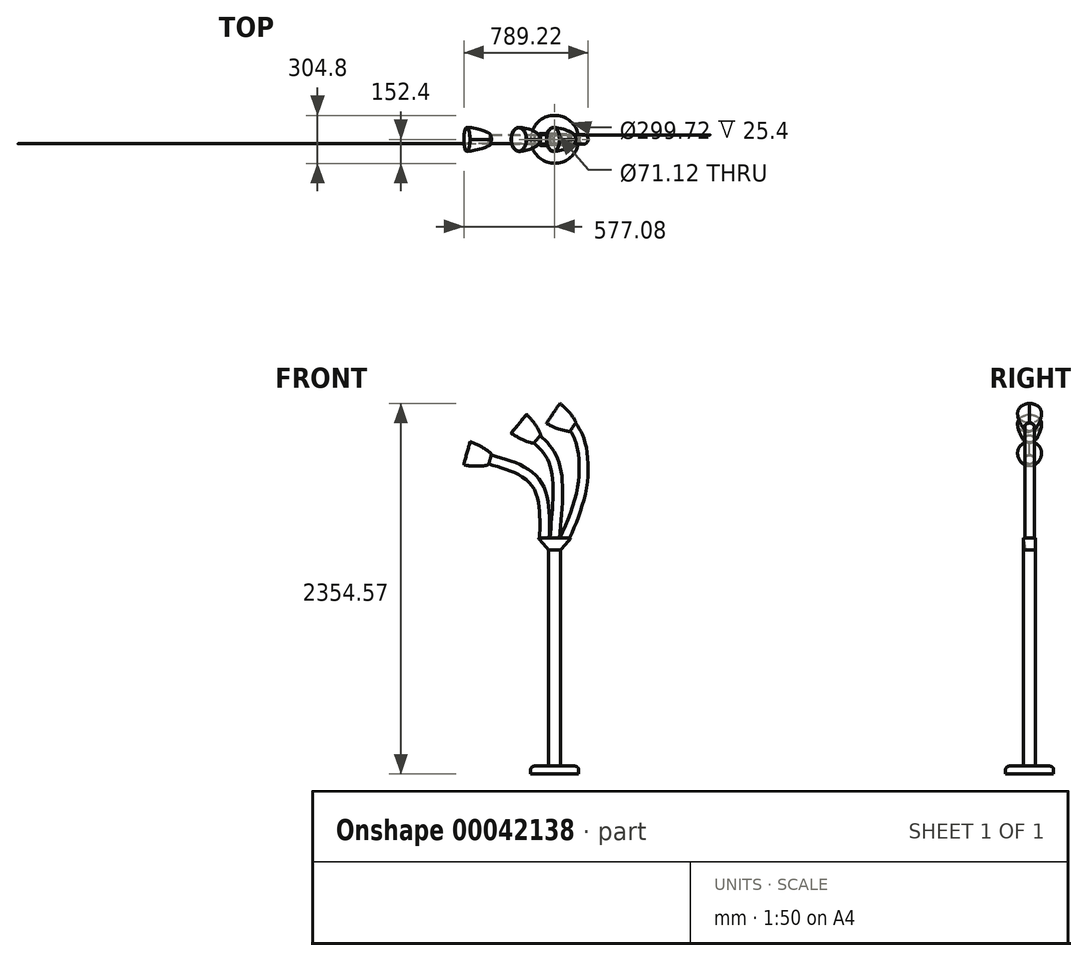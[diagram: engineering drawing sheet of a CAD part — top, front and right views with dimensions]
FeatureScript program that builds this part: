
annotation { "Feature Type Name" : "Feature", "Feature Type Description" : "" }
export const myFeature = defineFeature(function(context is Context, id is Id, definition is map)
    precondition{}
    {
        {
            var Q0;
            Q0=qCreatedBy(makeId("Top.planeOp"),FACE);
            var sketch = newSketch(context, id + "F0", { "sketchPlane" : qUnion([Q0])});
            skCircle(sketch, "E0", {"center": v(0, 0) * mm, "radius": 152.4 * mm});
            skSolve(sketch);
        }
        {
            var Q0;
            Q0=makeQuery(id+"F0.imprint","IMPRINT",FACE,{"disambiguationData":[TD([[makeQuery(id+"F0.imprint","IMPRINT",EDGE,{"derivedFrom":sQuery(id+"F0.wireOp",EDGE,"E0")}),1.0]])]});
            extrude(context, id + "F1", {"entities" : qUnion([Q0]), "depth" : 50.8 * mm});
        }
        {
            var Q0;
            Q0=makeQuery(id+"F1.opExtrude","CAP_EDGE",EDGE,{"disambiguationData":[OSD([sQuery(id+"F0.wireOp",EDGE,"E0")])],"isStart":false});
            fillet(context, id + "F2", {"entities" : qUnion([Q0]), "radius" : 22.86 * mm, "tangentPropagation" : true, "allowEdgeOverflow" : false});
        }
        {
            var Q0;
            Q0=makeQuery(id+"F1.opExtrude","CAP_FACE",FACE,{"disambiguationData":[OSD([sQuery(id+"F0.wireOp",EDGE,"E0")])],"isStart":false});
            var sketch = newSketch(context, id + "F3", { "sketchPlane" : qUnion([Q0])});
            skCircle(sketch, "E1", {"center": v(0, 0) * mm, "radius": 38.1 * mm});
            skSolve(sketch);
        }
        {
            var Q0;
            Q0=makeQuery(id+"F3.imprint","IMPRINT",FACE,{"disambiguationData":[TD([[makeQuery(id+"F3.imprint","IMPRINT",EDGE,{"derivedFrom":sQuery(id+"F3.wireOp",EDGE,"E1")}),1.0]])]});
            extrude(context, id + "F4", {"entities" : qUnion([Q0]), "operationType" : NewBodyOperationType.ADD, "depth" : 1371.6 * mm});
        }
        {
            var Q0;
            Q0=makeQuery(id+"F4.opExtrude","CAP_FACE",FACE,{"disambiguationData":[OSD([sQuery(id+"F3.wireOp",EDGE,"E1")])],"isStart":false});
            cPlane(context, id + "F5", {"entities" : qUnion([Q0]), "cplaneType" : CPlaneType.OFFSET, "offset" : 76.2 * mm, "width" : 152.4 * mm, "height" : 152.4 * mm});
        }
        {
            var Q0;
            Q0=qCreatedBy(id+"F5.planeOp",FACE);
            var sketch = newSketch(context, id + "F6", { "sketchPlane" : qUnion([Q0])});
            skLineSegment(sketch, "E2.bottom", {"start": v(0, 38.1) * mm, "end": v(0, 38.1) * mm});
            skLineSegment(sketch, "E2.top", {"start": v(0, -38.1) * mm, "end": v(0, -38.1) * mm});
            skLineSegment(sketch, "E2.left", {"start": v(0, 38.1) * mm, "end": v(0, -38.1) * mm, "construction": true});
            skLineSegment(sketch, "E2.right", {"start": v(0, 38.1) * mm, "end": v(0, -38.1) * mm, "construction": true});
            skLineSegment(sketch, "E3", {"start": v(0, 38.1) * mm, "end": v(88.9, 38.1) * mm});
            skLineSegment(sketch, "E4", {"start": v(101.6, 25.4) * mm, "end": v(101.6, -25.4) * mm});
            skLineSegment(sketch, "E5", {"start": v(88.9, -38.1) * mm, "end": v(0, -38.1) * mm});
            skLineSegment(sketch, "E6", {"start": v(0, -38.1) * mm, "end": v(-88.9, -38.1) * mm});
            skLineSegment(sketch, "E7", {"start": v(-101.6, -25.4) * mm, "end": v(-101.6, 25.4) * mm});
            skLineSegment(sketch, "E8", {"start": v(-88.9, 38.1) * mm, "end": v(0, 38.1) * mm});
            skPoint(sketch, "E9.visualSharp", {"position": v(101.6, 38.1) * mm});
            skArc(sketch, "E9.filletArc", {"start": v(101.6, 25.4) * mm, "mid": v(97.88, 34.38) * mm, "end": v(88.9, 38.1) * mm});
            skPoint(sketch, "E10.visualSharp", {"position": v(101.6, -38.1) * mm});
            skArc(sketch, "E10.filletArc", {"start": v(88.9, -38.1) * mm, "mid": v(97.88, -34.38) * mm, "end": v(101.6, -25.4) * mm});
            skPoint(sketch, "E11.visualSharp", {"position": v(-101.6, -38.1) * mm});
            skArc(sketch, "E11.filletArc", {"start": v(-101.6, -25.4) * mm, "mid": v(-97.88, -34.38) * mm, "end": v(-88.9, -38.1) * mm});
            skPoint(sketch, "E12.visualSharp", {"position": v(-101.6, 38.1) * mm});
            skArc(sketch, "E12.filletArc", {"start": v(-88.9, 38.1) * mm, "mid": v(-97.88, 34.38) * mm, "end": v(-101.6, 25.4) * mm});
            skSolve(sketch);
        }
        {
            var Q0;
            Q0=makeQuery(id+"F4.opExtrude","CAP_FACE",FACE,{"disambiguationData":[OSD([sQuery(id+"F3.wireOp",EDGE,"E1")])],"isStart":false});
            var sketch = newSketch(context, id + "F7", { "sketchPlane" : qUnion([Q0])});
            skArc(sketch, "E13", {"start": v(-27.2, 26.68) * mm, "mid": v(-38.1, 0.43) * mm, "end": v(-27.8, -26.06) * mm});
            skArc(sketch, "E14", {"start": v(-27.8, -26.06) * mm, "mid": v(1, -38.09) * mm, "end": v(29.12, -24.57) * mm});
            skArc(sketch, "E15", {"start": v(29.12, -24.57) * mm, "mid": v(38.04, 2.06) * mm, "end": v(26.3, 27.57) * mm});
            skArc(sketch, "E16", {"start": v(26.3, 27.57) * mm, "mid": v(-0.64, 38.1) * mm, "end": v(-27.2, 26.68) * mm});
            skSolve(sketch);
        }
        {
            var Q1;
            Q1=makeQuery(id+"F7.imprint","IMPRINT",FACE,{"disambiguationData":[TD([[makeQuery(id+"F7.imprint","IMPRINT",EDGE,{"derivedFrom":sQuery(id+"F7.wireOp",EDGE,"E13")}),1.0]])]});
            var Q2;
            Q2=makeQuery(id+"F6.imprint","IMPRINT",FACE,{"disambiguationData":[TD([[makeQuery(id+"F6.imprint","IMPRINT",EDGE,{"derivedFrom":sQuery(id+"F6.wireOp",EDGE,"E3")}),-1.0]])]});
            var Q3;
            Q3=sQuery(id+"F7.wireOp",VERTEX,"E15.start");
            var Q4;
            Q4=sQuery(id+"F6.wireOp",VERTEX,"E5.start");
            loft(context, id + "F8", {"operationType" : NewBodyOperationType.ADD, "sheetProfilesArray" : [{ "sheetProfileEntities" : qUnion([Q1]) }, { "sheetProfileEntities" : qUnion([Q2]) }], "matchConnections" : true, "connections" : [{ "connectionEntities" : qUnion([Q3, Q4]), "connectionEdgeQueries" : qUnion([]), "connectionEdgeParameters" : [] }]});
        }
        {
            var Q0;
            Q0=makeQuery(id+"F8.opLoft","CAP_FACE",FACE,{"disambiguationData":[OSD([makeQuery(id+"F6.imprint","IMPRINT",FACE,{"disambiguationData":[TD([[makeQuery(id+"F6.imprint","IMPRINT",EDGE,{"derivedFrom":sQuery(id+"F6.wireOp",EDGE,"E3")}),-1.0]])]})])],"isStart":true});
            var sketch = newSketch(context, id + "F9", { "sketchPlane" : qUnion([Q0])});
            skCircle(sketch, "E17", {"center": v(64.74, 0) * mm, "radius": 30.45 * mm});
            skCircle(sketch, "E18", {"center": v(0, 0) * mm, "radius": 30.45 * mm});
            skCircle(sketch, "E19", {"center": v(-64.74, 0) * mm, "radius": 30.45 * mm});
            skLineSegment(sketch, "E20", {"start": v(64.74, 0) * mm, "end": v(0, 0) * mm});
            skLineSegment(sketch, "E21", {"start": v(0, 0) * mm, "end": v(-64.74, 0) * mm});
            skSolve(sketch);
        }
        {
            var Q0;
            Q0=qCreatedBy(makeId("Front.planeOp"),FACE);
            var sketch = newSketch(context, id + "F10", { "sketchPlane" : qUnion([Q0])});
            skCircle(sketch, "E22", {"center": v(0, 0) * mm, "radius": 24.83 * mm});
            skCircle(sketch, "E23", {"center": v(-62.86, 0) * mm, "radius": 24.83 * mm});
            skCircle(sketch, "E24", {"center": v(62.86, 0) * mm, "radius": 24.83 * mm});
            skLineSegment(sketch, "E25", {"start": v(62.86, 0) * mm, "end": v(0, 0) * mm, "construction": true});
            skLineSegment(sketch, "E26", {"start": v(0, 0) * mm, "end": v(-62.86, 0) * mm, "construction": true});
            skFitSpline(sketch, "E27", {"points": [v(0, 1498.72) * mm, v(0, 1966.96) * mm, v(-110.42, 2128.4) * mm], "startDerivative": vector(85.42, 880.08) * mm, "endDerivative": vector(-336.47, 340.63) * mm});
            skFitSpline(sketch, "E28", {"points": [v(-64.74, 1498.6) * mm, v(-119.82, 1851.4) * mm, v(-410.2, 1998.5) * mm], "startDerivative": vector(15.1, 783.93) * mm, "endDerivative": vector(-712.02, 206.42) * mm});
            skFitSpline(sketch, "E29", {"points": [v(64.74, 1498.6) * mm, v(173.73, 1819.38) * mm, v(164.83, 2105.76) * mm, v(116.29, 2205.3) * mm], "startDerivative": vector(322.12, 770.87) * mm, "endDerivative": vector(-235.51, 362.9) * mm});
            skSolve(sketch);
        }
        {
            var Q0;
            Q0=makeQuery(id+"F9.imprint","IMPRINT",FACE,{"disambiguationData":[TD([[makeQuery(id+"F9.imprint","IMPRINT",EDGE,{"derivedFrom":sQuery(id+"F9.wireOp",EDGE,"E17")}),1.0]])]});
            var Q1;
            Q1=sQuery(id+"F10.wireOp",EDGE,"E29");
            sweep(context, id + "F11", {"operationType" : NewBodyOperationType.ADD, "profiles" : qUnion([Q0]), "path" : qUnion([Q1])});
        }
        {
            var Q0;
            {var subQ1=sQuery(id+"F9.wireOp",EDGE,"E18");var subQ3=sQuery(id+"F9.wireOp",EDGE,"E20");var subQ5=makeQuery(id+"F9.imprint","INTERSECT",VERTEX,{"derivedFrom":[subQ1,subQ3]});Q0=makeQuery(id+"F9.imprint","IMPRINT",FACE,{"disambiguationData":[TD([[makeQuery(id+"F9.imprint","IMPRINT",EDGE,{"disambiguationData":[TD([[subQ5,1.0]])],"derivedFrom":subQ1}),1.0]])]});}
            var Q1;
            {var subQ1=sQuery(id+"F9.wireOp",EDGE,"E18");var subQ3=sQuery(id+"F9.wireOp",EDGE,"E20");var subQ5=makeQuery(id+"F9.imprint","INTERSECT",VERTEX,{"derivedFrom":[subQ1,subQ3]});Q1=makeQuery(id+"F9.imprint","IMPRINT",FACE,{"disambiguationData":[TD([[makeQuery(id+"F9.imprint","IMPRINT",EDGE,{"disambiguationData":[TD([[subQ5,-1.0]])],"derivedFrom":subQ1}),1.0]])]});}
            var Q2;
            Q2=sQuery(id+"F10.wireOp",EDGE,"E27");
            sweep(context, id + "F12", {"operationType" : NewBodyOperationType.ADD, "profiles" : qUnion([Q0, Q1]), "path" : qUnion([Q2])});
        }
        {
            var Q0;
            Q0=makeQuery(id+"F9.imprint","IMPRINT",FACE,{"disambiguationData":[TD([[makeQuery(id+"F9.imprint","IMPRINT",EDGE,{"derivedFrom":sQuery(id+"F9.wireOp",EDGE,"E19")}),1.0]])]});
            var Q1;
            Q1=sQuery(id+"F10.wireOp",EDGE,"E28");
            sweep(context, id + "F13", {"operationType" : NewBodyOperationType.ADD, "profiles" : qUnion([Q0]), "path" : qUnion([Q1])});
        }
        {
            var Q0;
            Q0=makeQuery(id+"F11.opSweep","CAP_FACE",FACE,{"disambiguationData":[OSD([sQuery(id+"F9.wireOp",EDGE,"E17"),sQuery(id+"F10.wireOp",VERTEX,"E29.end")])],"isStart":false});
            cPlane(context, id + "F14", {"entities" : qUnion([Q0]), "cplaneType" : CPlaneType.OFFSET, "offset" : 152.4 * mm, "width" : 152.4 * mm, "height" : 152.4 * mm});
        }
        {
            var Q0;
            Q0=qCreatedBy(id+"F14.planeOp",FACE);
            var sketch = newSketch(context, id + "F15", { "sketchPlane" : qUnion([Q0])});
            skCircle(sketch, "E30", {"center": v(-0.19, 1887) * mm, "radius": 76.2 * mm});
            skSolve(sketch);
        }
        {
            var Q1;
            Q1=makeQuery(id+"F11.opSweep","CAP_FACE",FACE,{"disambiguationData":[OSD([sQuery(id+"F9.wireOp",EDGE,"E17"),sQuery(id+"F10.wireOp",VERTEX,"E29.end")])],"isStart":false});
            var Q2;
            Q2=makeQuery(id+"F15.imprint","IMPRINT",FACE,{"disambiguationData":[TD([[makeQuery(id+"F15.imprint","IMPRINT",EDGE,{"derivedFrom":sQuery(id+"F15.wireOp",EDGE,"E30")}),1.0]])]});
            loft(context, id + "F16", {"startCondition" : LoftEndDerivativeType.TANGENT_TO_PROFILE, "startMagnitude" : 1, "endCondition" : LoftEndDerivativeType.NORMAL_TO_PROFILE, "endMagnitude" : 1, "sheetProfilesArray" : [{ "sheetProfileEntities" : qUnion([Q1]) }, { "sheetProfileEntities" : qUnion([Q2]) }]});
        }
        {
            var Q0;
            Q0=makeQuery(id+"F12.opSweep","CAP_FACE",FACE,{"disambiguationData":[OSD([sQuery(id+"F9.wireOp",EDGE,"E18"),sQuery(id+"F10.wireOp",VERTEX,"E27.end")])],"isStart":false});
            cPlane(context, id + "F17", {"entities" : qUnion([Q0]), "cplaneType" : CPlaneType.OFFSET, "offset" : 152.4 * mm, "width" : 152.4 * mm, "height" : 152.4 * mm});
        }
        {
            var Q0;
            Q0=qCreatedBy(id+"F17.planeOp",FACE);
            var sketch = newSketch(context, id + "F18", { "sketchPlane" : qUnion([Q0])});
            skCircle(sketch, "E31", {"center": v(0.03, 1564.34) * mm, "radius": 76.2 * mm});
            skSolve(sketch);
        }
        {
            var Q0;
            Q0=makeQuery(id+"F13.opSweep","CAP_FACE",FACE,{"disambiguationData":[OSD([sQuery(id+"F9.wireOp",EDGE,"E19"),sQuery(id+"F10.wireOp",VERTEX,"E28.end")])],"isStart":false});
            cPlane(context, id + "F19", {"entities" : qUnion([Q0]), "cplaneType" : CPlaneType.OFFSET, "offset" : 152.4 * mm, "width" : 152.4 * mm, "height" : 152.4 * mm});
        }
        {
            var Q0;
            Q0=qCreatedBy(id+"F19.planeOp",FACE);
            var sketch = newSketch(context, id + "F20", { "sketchPlane" : qUnion([Q0])});
            skCircle(sketch, "E32", {"center": v(-0.07, 1823.6) * mm, "radius": 76.2 * mm});
            skSolve(sketch);
        }
        {
            var Q1;
            Q1=makeQuery(id+"F12.opSweep","CAP_FACE",FACE,{"disambiguationData":[OSD([sQuery(id+"F9.wireOp",EDGE,"E18"),sQuery(id+"F10.wireOp",VERTEX,"E27.end")])],"isStart":false});
            var Q2;
            Q2=makeQuery(id+"F18.imprint","IMPRINT",FACE,{"disambiguationData":[TD([[makeQuery(id+"F18.imprint","IMPRINT",EDGE,{"derivedFrom":sQuery(id+"F18.wireOp",EDGE,"E31")}),1.0]])]});
            loft(context, id + "F21", {"operationType" : NewBodyOperationType.ADD, "startCondition" : LoftEndDerivativeType.TANGENT_TO_PROFILE, "startMagnitude" : 1, "endCondition" : LoftEndDerivativeType.NORMAL_TO_PROFILE, "endMagnitude" : 1, "sheetProfilesArray" : [{ "sheetProfileEntities" : qUnion([Q1]) }, { "sheetProfileEntities" : qUnion([Q2]) }]});
        }
        {
            var Q1;
            Q1=makeQuery(id+"F13.opSweep","CAP_FACE",FACE,{"disambiguationData":[OSD([sQuery(id+"F9.wireOp",EDGE,"E19"),sQuery(id+"F10.wireOp",VERTEX,"E28.end")])],"isStart":false});
            var Q2;
            Q2=makeQuery(id+"F20.imprint","IMPRINT",FACE,{"disambiguationData":[TD([[makeQuery(id+"F20.imprint","IMPRINT",EDGE,{"derivedFrom":sQuery(id+"F20.wireOp",EDGE,"E32")}),1.0]])]});
            loft(context, id + "F22", {"startCondition" : LoftEndDerivativeType.TANGENT_TO_PROFILE, "startMagnitude" : 1, "endCondition" : LoftEndDerivativeType.NORMAL_TO_PROFILE, "endMagnitude" : 1, "sheetProfilesArray" : [{ "sheetProfileEntities" : qUnion([Q1]) }, { "sheetProfileEntities" : qUnion([Q2]) }]});
        }
        {
            var Q0;
            Q0=makeQuery(id+"F22.opLoft","CAP_FACE",FACE,{"disambiguationData":[OSD([makeQuery(id+"F20.imprint","IMPRINT",FACE,{"disambiguationData":[TD([[makeQuery(id+"F20.imprint","IMPRINT",EDGE,{"derivedFrom":sQuery(id+"F20.wireOp",EDGE,"E32")}),1.0]])]})])],"isStart":true});
            var Q1;
            Q1=makeQuery(id+"F21.opLoft","CAP_FACE",FACE,{"disambiguationData":[OSD([makeQuery(id+"F18.imprint","IMPRINT",FACE,{"disambiguationData":[TD([[makeQuery(id+"F18.imprint","IMPRINT",EDGE,{"derivedFrom":sQuery(id+"F18.wireOp",EDGE,"E31")}),1.0]])]})])],"isStart":true});
            var Q2;
            Q2=makeQuery(id+"F16.opLoft","CAP_FACE",FACE,{"disambiguationData":[OSD([makeQuery(id+"F15.imprint","IMPRINT",FACE,{"disambiguationData":[TD([[makeQuery(id+"F15.imprint","IMPRINT",EDGE,{"derivedFrom":sQuery(id+"F15.wireOp",EDGE,"E30")}),1.0]])]})])],"isStart":true});
            shell(context, id + "F23", {"entities" : qUnion([Q0, Q1, Q2]), "thickness" : 2.54 * mm});
        }
    });
